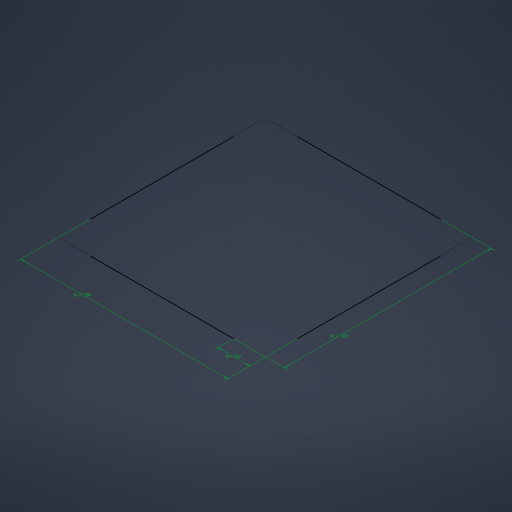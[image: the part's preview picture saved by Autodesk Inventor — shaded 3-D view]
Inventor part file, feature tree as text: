
AUTODESK INVENTOR PART (.ipt)
format: ipt  version: 2023.1 (Build 271208000, 208)  size: 175,616 bytes
history: native  units: in
note: dims shown in document units (in); Inventor stores cm internally (conversion verified against a paired STEP export)
features: other x1, sketch x1
ambient origin geometry x8: Origin, YZ Plane, XZ Plane, XY Plane, X Axis, Y Axis, Z Axis, Center Point
feature tree (2):
  parser-record x1  (decoder bookkeeping rows leaked as tree rows — omitted from the tree; the rows remain in map.json)
  sketch  "Sketch1"  dims[d1=27.5in d2=27.5in d3=4.25in]
note: 1 file-system path scrubbed to <path> (originals preserved in map.json)
